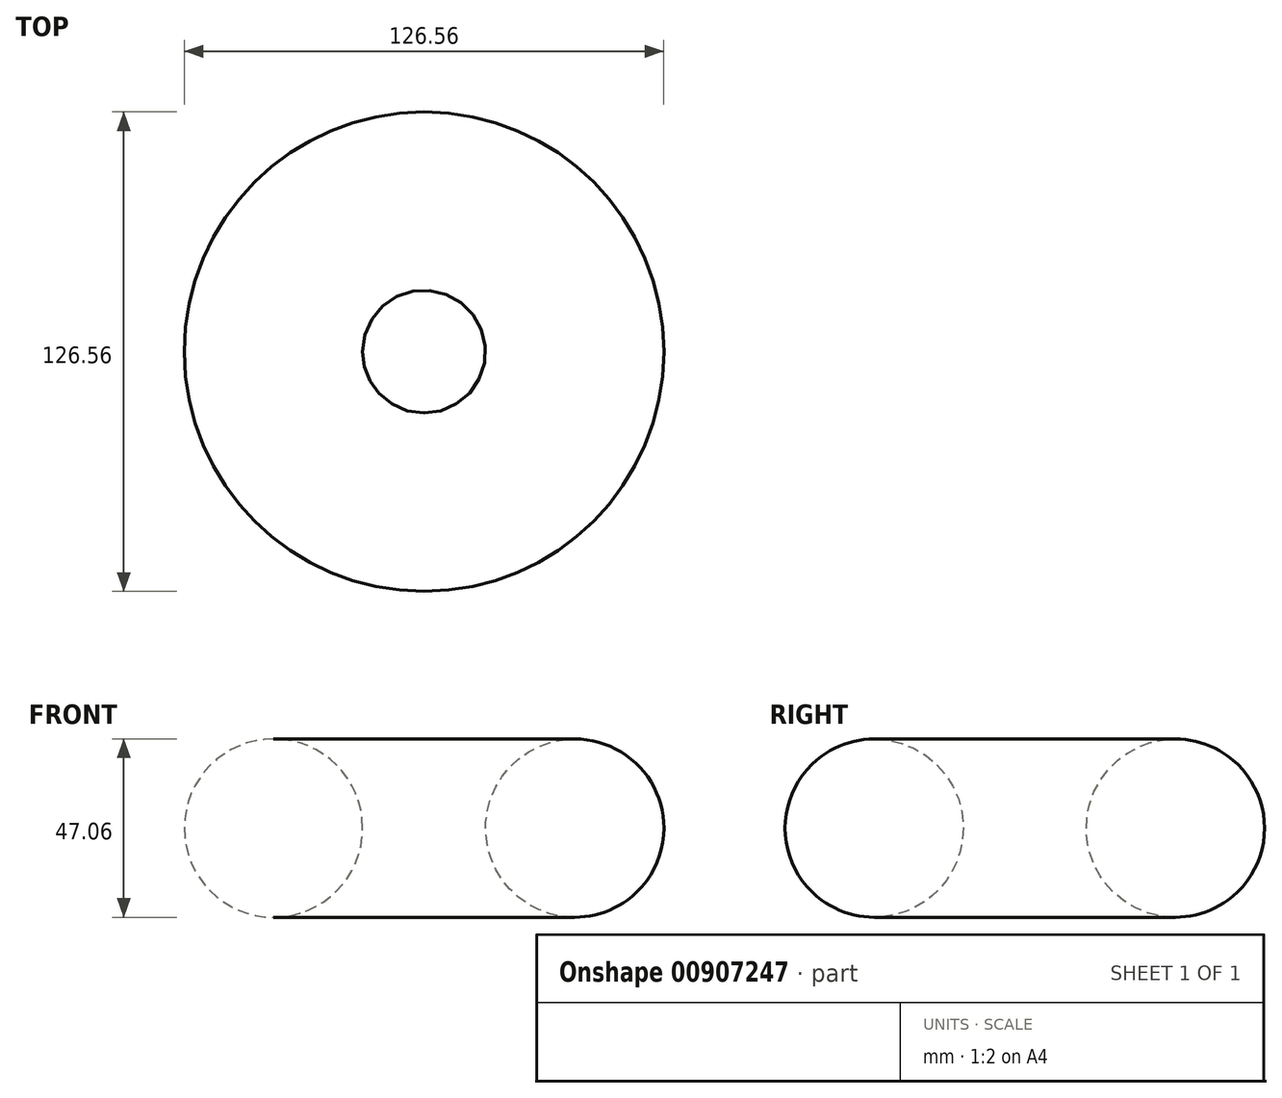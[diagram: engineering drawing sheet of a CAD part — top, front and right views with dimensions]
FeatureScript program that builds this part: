
annotation { "Feature Type Name" : "Feature", "Feature Type Description" : "" }
export const myFeature = defineFeature(function(context is Context, id is Id, definition is map)
    precondition{}
    {
        {
            var Q0;
            Q0=qCreatedBy(makeId("Front.planeOp"),FACE);
            var sketch = newSketch(context, id + "F0", { "sketchPlane" : qUnion([Q0])});
            skCircle(sketch, "E0", {"center": v(39.75, 0) * mm, "radius": 23.53 * mm});
            skSolve(sketch);
        }
        {
            var Q0;
            Q0=qCreatedBy(makeId("Front.planeOp"),FACE);
            var sketch = newSketch(context, id + "F1", { "sketchPlane" : qUnion([Q0])});
            skLineSegment(sketch, "E1", {"start": v(0, 0) * mm, "end": v(0, 58.11) * mm});
            skSolve(sketch);
        }
        {
            var Q0;
            Q0 = qSketchRegion(id + "F1", true);
            var Q1;
            Q1=makeQuery(id+"F0.imprint","IMPRINT",FACE,{"disambiguationData":[TD([[makeQuery(id+"F0.imprint","IMPRINT",EDGE,{"derivedFrom":sQuery(id+"F0.wireOp",EDGE,"E0")}),1.0]])]});
            var Q2;
            Q2=sQuery(id+"F1.wireOp",EDGE,"E1");
            revolve(context, id + "F2", {"surfaceOperationType" : NewSurfaceOperationType.NEW, "entities" : qUnion([Q0, Q1]), "axis" : qUnion([Q2]), "revolveType" : RevolveType.FULL});
        }
    });
